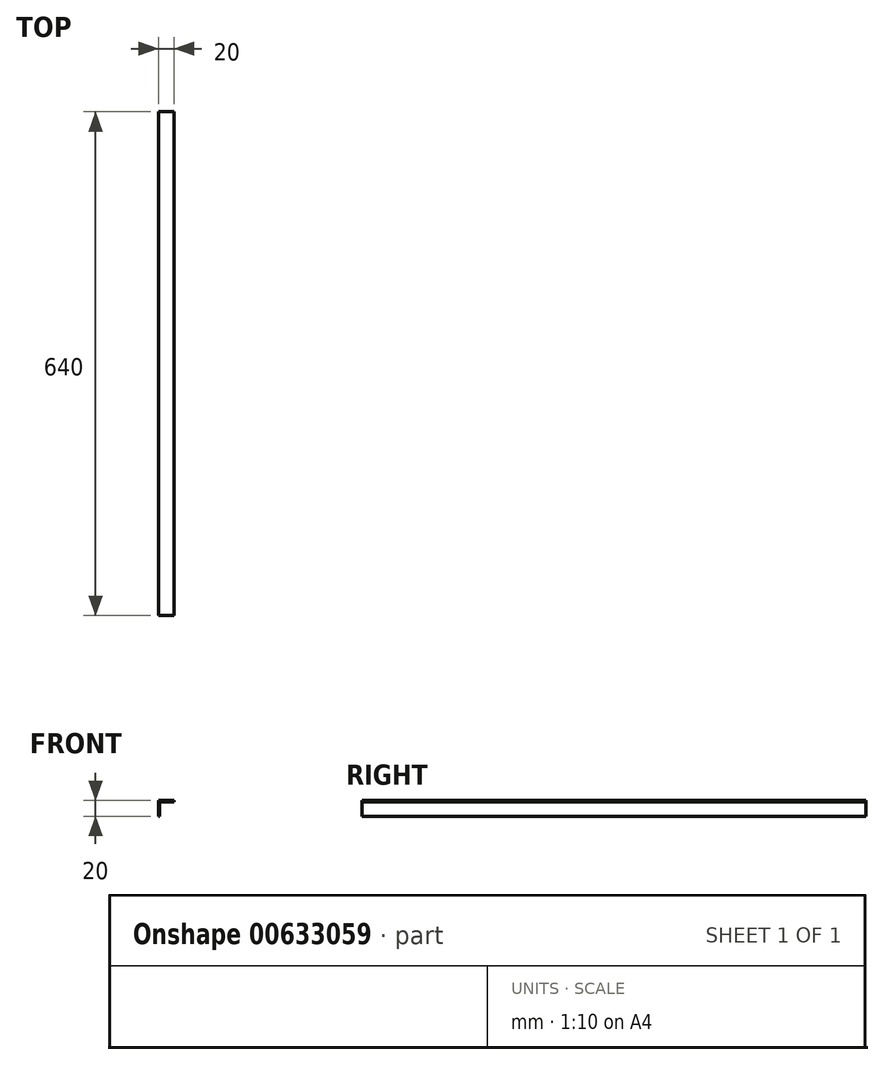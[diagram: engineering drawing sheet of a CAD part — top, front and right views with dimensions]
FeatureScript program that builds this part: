
annotation { "Feature Type Name" : "Feature", "Feature Type Description" : "" }
export const myFeature = defineFeature(function(context is Context, id is Id, definition is map)
    precondition{}
    {
        {
            var Q0;
            Q0=qCreatedBy(makeId("Front.planeOp"),FACE);
            var sketch = newSketch(context, id + "F0", { "sketchPlane" : qUnion([Q0])});
            skLineSegment(sketch, "E0", {"start": v(20, 0) * mm, "end": v(0, 0) * mm});
            skLineSegment(sketch, "E1", {"start": v(0, 0) * mm, "end": v(0, -20) * mm});
            skLineSegment(sketch, "E2", {"start": v(0, -20) * mm, "end": v(1.5, -20) * mm});
            skLineSegment(sketch, "E3", {"start": v(1.5, -20) * mm, "end": v(1.5, -1.5) * mm});
            skLineSegment(sketch, "E4", {"start": v(1.5, -1.5) * mm, "end": v(20, -1.5) * mm});
            skLineSegment(sketch, "E5", {"start": v(20, -1.5) * mm, "end": v(20, 0) * mm});
            skSolve(sketch);
        }
        {
            var Q0;
            Q0=makeQuery(id+"F0.imprint","IMPRINT",FACE,{"disambiguationData":[TD([[makeQuery(id+"F0.imprint","IMPRINT",EDGE,{"derivedFrom":sQuery(id+"F0.wireOp",EDGE,"E0")}),1.0]])]});
            extrude(context, id + "F1", {"entities" : qUnion([Q0]), "depth" : 640 * mm, "offsetDistance" : 25 * mm});
        }
    });
